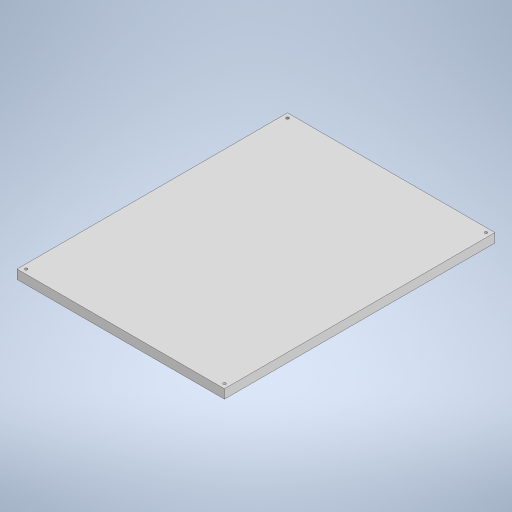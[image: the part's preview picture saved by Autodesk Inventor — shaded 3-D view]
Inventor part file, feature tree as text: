
AUTODESK INVENTOR PART (.ipt)
format: ipt  version: 2024 (Build 280153000, 153)  size: 261,632 bytes
history: native  units: mm
features: extrude x1, sketch x1
ambient origin geometry x8: Origin, YZ Plane, XZ Plane, XY Plane, X Axis, Y Axis, Z Axis, Center Point
bodies: Solido1 (feature_tree)
feature tree (2):
  extrude  "Estrusione1"  Depth=230.0mm
  sketch  "Schizzo1"
